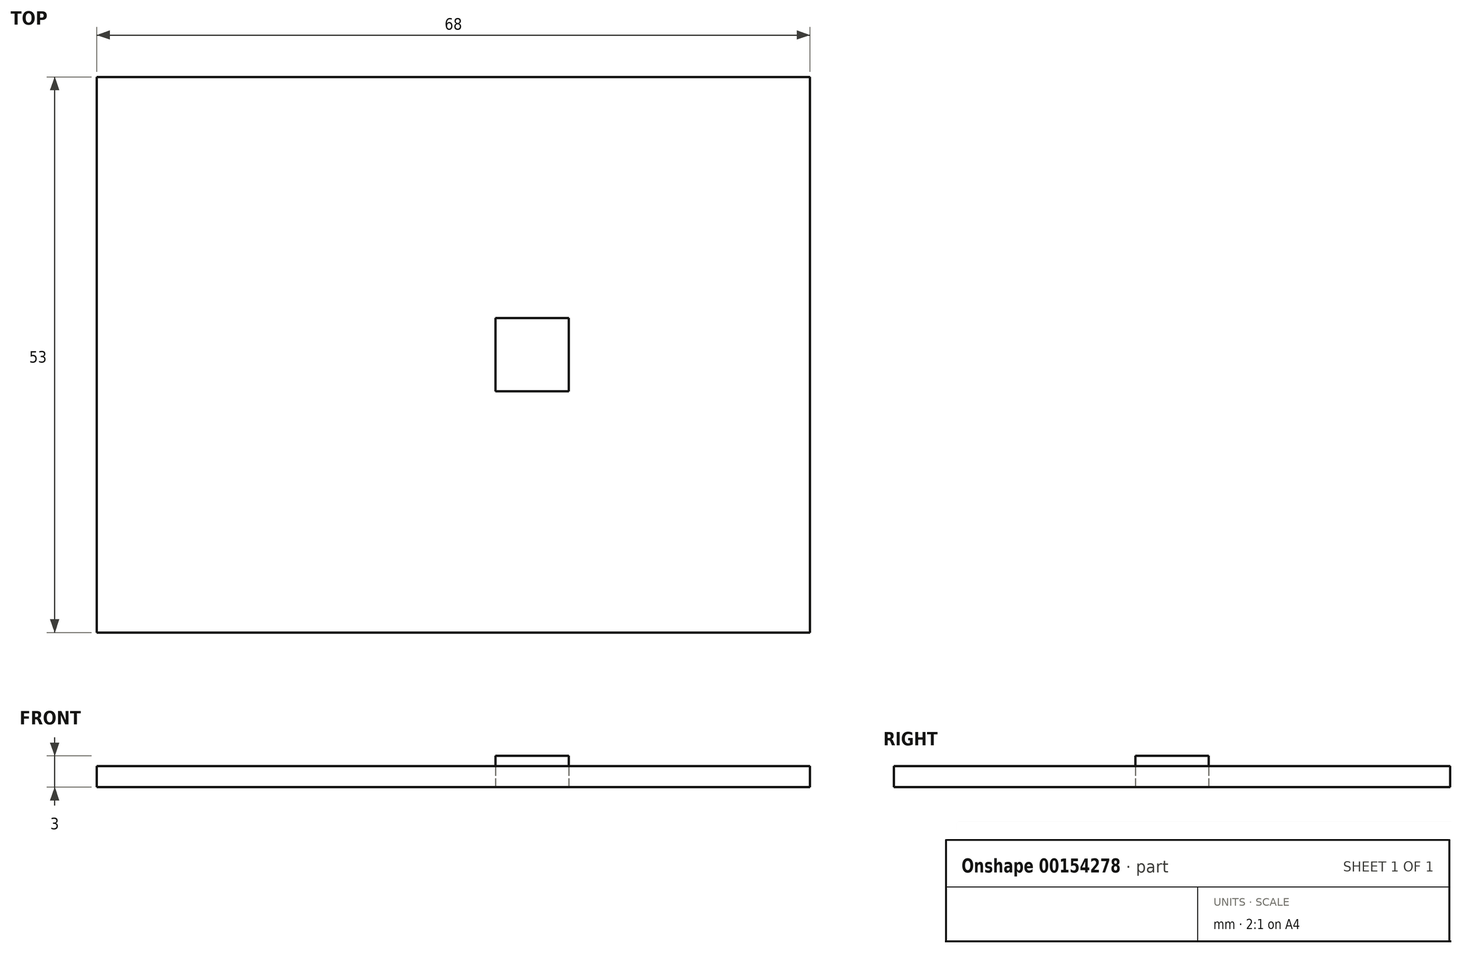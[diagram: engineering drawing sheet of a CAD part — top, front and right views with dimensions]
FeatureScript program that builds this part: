
annotation { "Feature Type Name" : "Feature", "Feature Type Description" : "" }
export const myFeature = defineFeature(function(context is Context, id is Id, definition is map)
    precondition{}
    {
        {
            var Q0;
            Q0=qCreatedBy(makeId("Top.planeOp"),FACE);
            var sketch = newSketch(context, id + "F0", { "sketchPlane" : qUnion([Q0])});
            skLineSegment(sketch, "E0.bottom", {"start": v(-34, 26.5) * mm, "end": v(34, 26.5) * mm});
            skLineSegment(sketch, "E0.top", {"start": v(-34, -26.5) * mm, "end": v(34, -26.5) * mm});
            skLineSegment(sketch, "E0.left", {"start": v(-34, 26.5) * mm, "end": v(-34, -26.5) * mm});
            skLineSegment(sketch, "E0.right", {"start": v(34, 26.5) * mm, "end": v(34, -26.5) * mm});
            skSolve(sketch);
        }
        {
            var Q0;
            Q0 = qSketchRegion(id + "F0", true);
            extrude(context, id + "F1", {"entities" : qUnion([Q0]), "depth" : 2 * mm});
        }
        {
            var Q0;
            Q0=makeQuery(id+"F0.imprint","IMPRINT",FACE,{"disambiguationData":[TD([[makeQuery(id+"F0.imprint","IMPRINT",EDGE,{"derivedFrom":sQuery(id+"F0.wireOp",EDGE,"E0.bottom")}),-1.0]])]});
            var sketch = newSketch(context, id + "F2", { "sketchPlane" : qUnion([Q0])});
            skLineSegment(sketch, "E1.bottom", {"start": v(4, 3.5) * mm, "end": v(11, 3.5) * mm});
            skLineSegment(sketch, "E1.top", {"start": v(4, -3.5) * mm, "end": v(11, -3.5) * mm});
            skLineSegment(sketch, "E1.left", {"start": v(4, 3.5) * mm, "end": v(4, -3.5) * mm});
            skLineSegment(sketch, "E1.right", {"start": v(11, 3.5) * mm, "end": v(11, -3.5) * mm});
            skSolve(sketch);
        }
        {
            var Q0;
            Q0=makeQuery(id+"F2.imprint","IMPRINT",FACE,{"disambiguationData":[TD([[makeQuery(id+"F2.imprint","IMPRINT",EDGE,{"derivedFrom":sQuery(id+"F2.wireOp",EDGE,"E1.bottom")}),-1.0]])]});
            extrude(context, id + "F3", {"entities" : qUnion([Q0]), "depth" : 3 * mm});
        }
    });
